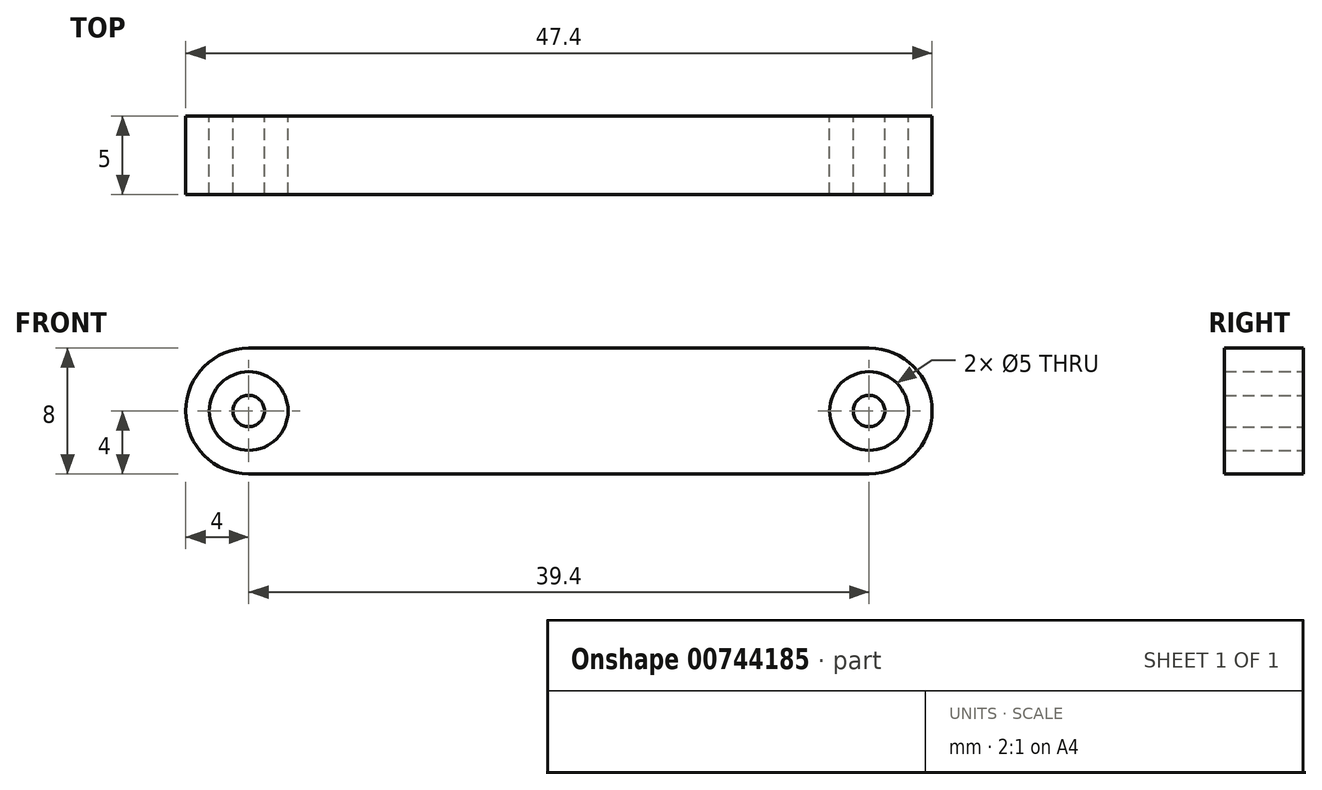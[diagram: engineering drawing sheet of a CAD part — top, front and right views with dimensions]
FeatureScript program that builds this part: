
annotation { "Feature Type Name" : "Feature", "Feature Type Description" : "" }
export const myFeature = defineFeature(function(context is Context, id is Id, definition is map)
    precondition{}
    {
        {
            var Q0;
            Q0=qCreatedBy(makeId("Front.planeOp"),FACE);
            var sketch = newSketch(context, id + "F0", { "sketchPlane" : qUnion([Q0])});
            skCircle(sketch, "E0", {"center": v(0, 0) * mm, "radius": 4 * mm});
            skCircle(sketch, "E1", {"center": v(39.4, 0) * mm, "radius": 4 * mm});
            skLineSegment(sketch, "E2", {"start": v(39.4, 4) * mm, "end": v(0, 4) * mm});
            skLineSegment(sketch, "E3", {"start": v(0, -4) * mm, "end": v(39.4, -4) * mm});
            skCircle(sketch, "E4", {"center": v(0, 0) * mm, "radius": 2.5 * mm});
            skCircle(sketch, "E5", {"center": v(39.4, 0) * mm, "radius": 2.5 * mm});
            skCircle(sketch, "E6", {"center": v(39.4, 0) * mm, "radius": 1 * mm});
            skCircle(sketch, "E7", {"center": v(0, 0) * mm, "radius": 1 * mm});
            skSolve(sketch);
        }
        {
            var Q0;
            Q0=qSketchRegion(id+"F0",true);
            var Q1;
            Q1=makeQuery(id+"F0.imprint","IMPRINT",FACE,{"disambiguationData":[TD([[makeQuery(id+"F0.imprint","IMPRINT",EDGE,{"derivedFrom":sQuery(id+"F0.wireOp",EDGE,"E7")}),1.0]])]});
            var Q2;
            Q2=makeQuery(id+"F0.imprint","IMPRINT",FACE,{"disambiguationData":[TD([[makeQuery(id+"F0.imprint","IMPRINT",EDGE,{"derivedFrom":sQuery(id+"F0.wireOp",EDGE,"E6")}),1.0]])]});
            extrude(context, id + "F1", {"entities" : qUnion([Q0, Q1, Q2]), "depth" : 5 * mm, "offsetDistance" : 25 * mm});
        }
    });
